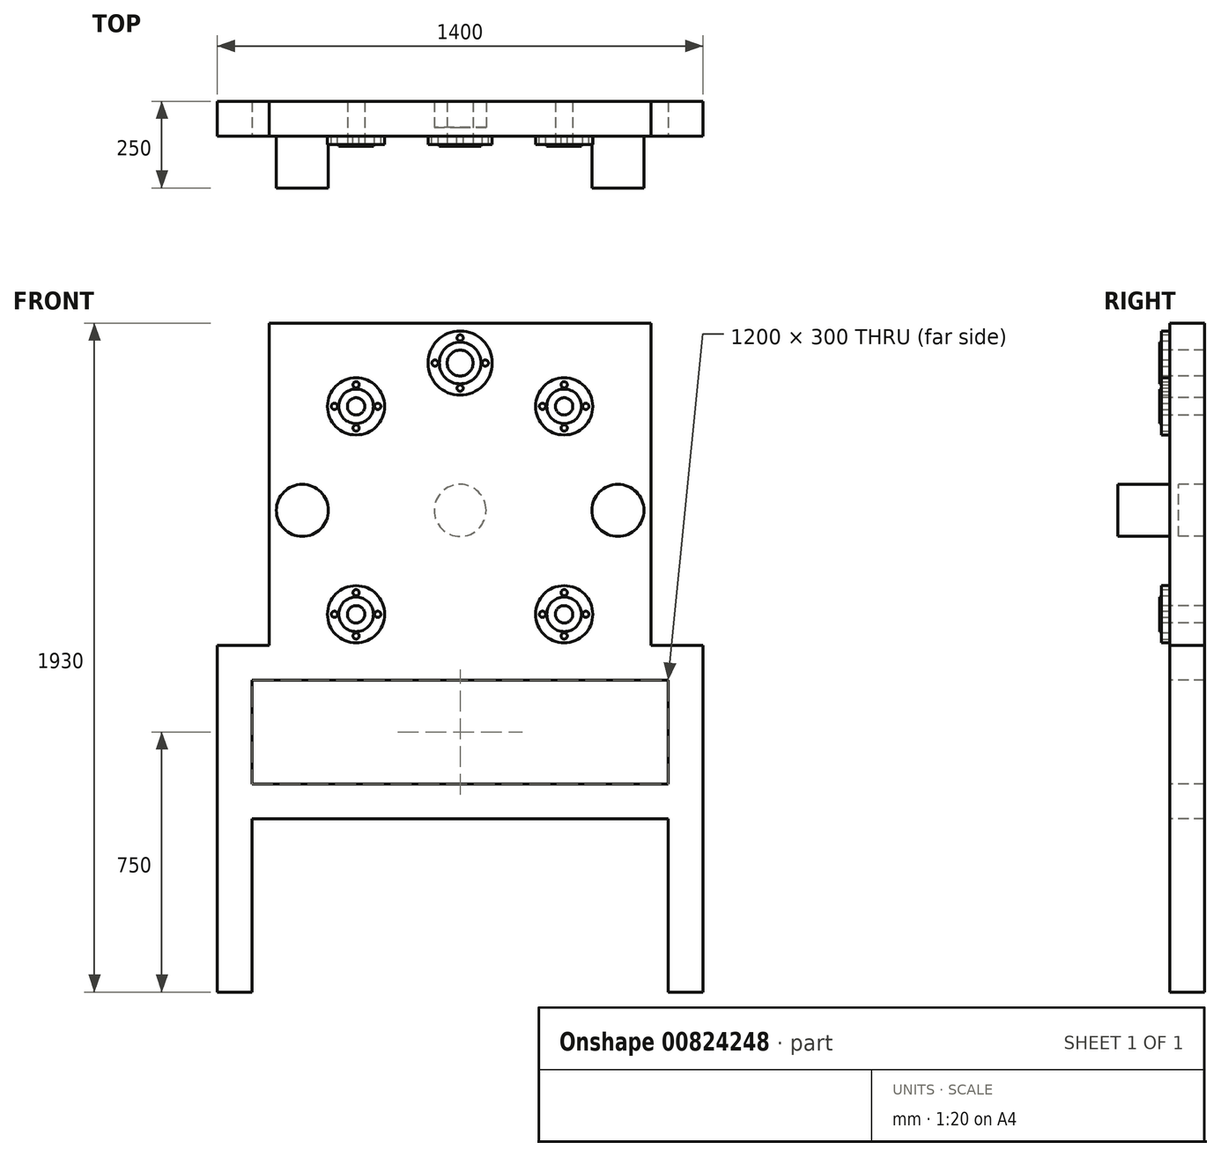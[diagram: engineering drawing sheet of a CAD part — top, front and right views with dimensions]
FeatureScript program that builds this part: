
annotation { "Feature Type Name" : "Feature", "Feature Type Description" : "" }
export const myFeature = defineFeature(function(context is Context, id is Id, definition is map)
    precondition{}
    {
        {
            var Q0;
            Q0=qCreatedBy(makeId("Front.planeOp"),FACE);
            var sketch = newSketch(context, id + "F0", { "sketchPlane" : qUnion([Q0])});
            skLineSegment(sketch, "E0.bottom", {"start": v(550, -965) * mm, "end": v(400, -965) * mm});
            skLineSegment(sketch, "E0.top", {"start": v(550, 965) * mm, "end": v(-550, 965) * mm});
            skLineSegment(sketch, "E0.left", {"start": v(550, -965) * mm, "end": v(550, 965) * mm});
            skLineSegment(sketch, "E0.right", {"start": v(-550, -965) * mm, "end": v(-550, 965) * mm});
            skPoint(sketch, "E0.middle", {"position": v(0, 0) * mm});
            skLineSegment(sketch, "E1.top", {"start": v(-400, -765) * mm, "end": v(400, -765) * mm});
            skLineSegment(sketch, "E1.left", {"start": v(-400, -965) * mm, "end": v(-400, -765) * mm});
            skLineSegment(sketch, "E1.right", {"start": v(400, -965) * mm, "end": v(400, -765) * mm});
            skLineSegment(sketch, "E2.bottom", {"start": v(-400, -615) * mm, "end": v(400, -615) * mm});
            skLineSegment(sketch, "E2.top", {"start": v(-400, -315) * mm, "end": v(400, -315) * mm});
            skLineSegment(sketch, "E2.left", {"start": v(-400, -615) * mm, "end": v(-400, -315) * mm});
            skLineSegment(sketch, "E2.right", {"start": v(400, -615) * mm, "end": v(400, -315) * mm});
            skLineSegment(sketch, "E3.trimOffspring", {"start": v(-400, -965) * mm, "end": v(-550, -965) * mm});
            skLineSegment(sketch, "E4.bottom", {"start": v(-400, -165) * mm, "end": v(400, -165) * mm});
            skLineSegment(sketch, "E4.top", {"start": v(-400, 35) * mm, "end": v(400, 35) * mm});
            skLineSegment(sketch, "E4.left", {"start": v(-400, -165) * mm, "end": v(-400, 35) * mm});
            skLineSegment(sketch, "E4.right", {"start": v(400, -165) * mm, "end": v(400, 35) * mm});
            skPoint(sketch, "E5.middle", {"position": v(0, 425) * mm});
            skSolve(sketch);
        }
        {
            var Q0;
            Q0=makeQuery(id+"F0.imprint","IMPRINT",FACE,{"disambiguationData":[TD([[makeQuery(id+"F0.imprint","IMPRINT",EDGE,{"derivedFrom":sQuery(id+"F0.wireOp",EDGE,"E0.bottom")}),-1.0]])]});
            extrude(context, id + "F1", {"entities" : qUnion([Q0]), "depth" : 100 * mm, "offsetDistance" : 25 * mm});
        }
        {
            var Q0;
            Q0=makeQuery(id+"F1.opExtrude","CAP_FACE",FACE,{"disambiguationData":[OSD([sQuery(id+"F0.wireOp",EDGE,"E0.bottom"),sQuery(id+"F0.wireOp",EDGE,"E0.top"),sQuery(id+"F0.wireOp",EDGE,"E0.left"),sQuery(id+"F0.wireOp",EDGE,"E0.right"),sQuery(id+"F0.wireOp",EDGE,"E1.top"),sQuery(id+"F0.wireOp",EDGE,"E1.left"),sQuery(id+"F0.wireOp",EDGE,"E1.right"),sQuery(id+"F0.wireOp",EDGE,"E2.bottom"),sQuery(id+"F0.wireOp",EDGE,"E2.top"),sQuery(id+"F0.wireOp",EDGE,"E2.left"),sQuery(id+"F0.wireOp",EDGE,"E2.right"),sQuery(id+"F0.wireOp",EDGE,"E3.trimOffspring"),sQuery(id+"F0.wireOp",EDGE,"nSGubIzk-R7de-6MO4-penA-cvBglKJnvsGC"),sQuery(id+"F0.wireOp",EDGE,"E4.bottom"),sQuery(id+"F0.wireOp",EDGE,"E4.top"),sQuery(id+"F0.wireOp",EDGE,"E4.left"),sQuery(id+"F0.wireOp",EDGE,"E4.right")])],"isStart":false});
            var sketch = newSketch(context, id + "F2", { "sketchPlane" : qUnion([Q0])});
            skCircle(sketch, "E6", {"center": v(-300, 125) * mm, "radius": 25 * mm});
            skCircle(sketch, "E7.0", {"center": v(0, 425) * mm, "radius": 75 * mm});
            skCircle(sketch, "E8.0.1.0", {"center": v(-300, 725) * mm, "radius": 25 * mm});
            skCircle(sketch, "E8.1.0.0", {"center": v(300, 125) * mm, "radius": 25 * mm});
            skCircle(sketch, "E8.1.1.0", {"center": v(300, 725) * mm, "radius": 25 * mm});
            skLineSegment(sketch, "E8.direction1", {"start": v(-300, 125) * mm, "end": v(300, 125) * mm, "construction": true});
            skLineSegment(sketch, "E8.direction2", {"start": v(-300, 125) * mm, "end": v(-300, 725) * mm, "construction": true});
            skSolve(sketch);
        }
        {
            var Q0;
            Q0=qSketchRegion(id+"F2",true);
            extrude(context, id + "F3", {"entities" : qUnion([Q0]), "operationType" : NewBodyOperationType.REMOVE, "oppositeDirection" : true, "depth" : 100 * mm, "offsetDistance" : 25 * mm});
        }
        {
            var Q0;
            Q0=makeQuery(id+"F1.opExtrude","CAP_FACE",FACE,{"disambiguationData":[OSD([sQuery(id+"F0.wireOp",EDGE,"E0.bottom"),sQuery(id+"F0.wireOp",EDGE,"E0.top"),sQuery(id+"F0.wireOp",EDGE,"E0.left"),sQuery(id+"F0.wireOp",EDGE,"E0.right"),sQuery(id+"F0.wireOp",EDGE,"E1.top"),sQuery(id+"F0.wireOp",EDGE,"E1.left"),sQuery(id+"F0.wireOp",EDGE,"E1.right"),sQuery(id+"F0.wireOp",EDGE,"E2.bottom"),sQuery(id+"F0.wireOp",EDGE,"E2.top"),sQuery(id+"F0.wireOp",EDGE,"E2.left"),sQuery(id+"F0.wireOp",EDGE,"E2.right"),sQuery(id+"F0.wireOp",EDGE,"E3.trimOffspring"),sQuery(id+"F0.wireOp",EDGE,"nSGubIzk-R7de-6MO4-penA-cvBglKJnvsGC"),sQuery(id+"F0.wireOp",EDGE,"E4.bottom"),sQuery(id+"F0.wireOp",EDGE,"E4.top"),sQuery(id+"F0.wireOp",EDGE,"E4.left"),sQuery(id+"F0.wireOp",EDGE,"E4.right")])],"isStart":false});
            var sketch = newSketch(context, id + "F4", { "sketchPlane" : qUnion([Q0])});
            skCircle(sketch, "E9", {"center": v(-455, 425) * mm, "radius": 75 * mm});
            skCircle(sketch, "E10.MirrorC", {"center": v(455, 425) * mm, "radius": 75 * mm});
            skSolve(sketch);
        }
        {
            var Q0;
            Q0=qSketchRegion(id+"F4",true);
            extrude(context, id + "F5", {"entities" : qUnion([Q0]), "operationType" : NewBodyOperationType.ADD, "depth" : 150 * mm, "offsetDistance" : 25 * mm});
        }
        {
            var Q0;
            Q0=makeQuery(id+"F1.opExtrude","CAP_FACE",FACE,{"disambiguationData":[OSD([sQuery(id+"F0.wireOp",EDGE,"E0.bottom"),sQuery(id+"F0.wireOp",EDGE,"E0.top"),sQuery(id+"F0.wireOp",EDGE,"E0.left"),sQuery(id+"F0.wireOp",EDGE,"E0.right"),sQuery(id+"F0.wireOp",EDGE,"E1.top"),sQuery(id+"F0.wireOp",EDGE,"E1.left"),sQuery(id+"F0.wireOp",EDGE,"E1.right"),sQuery(id+"F0.wireOp",EDGE,"E2.bottom"),sQuery(id+"F0.wireOp",EDGE,"E2.top"),sQuery(id+"F0.wireOp",EDGE,"E2.left"),sQuery(id+"F0.wireOp",EDGE,"E2.right"),sQuery(id+"F0.wireOp",EDGE,"E3.trimOffspring"),sQuery(id+"F0.wireOp",EDGE,"nSGubIzk-R7de-6MO4-penA-cvBglKJnvsGC"),sQuery(id+"F0.wireOp",EDGE,"E4.bottom"),sQuery(id+"F0.wireOp",EDGE,"E4.top"),sQuery(id+"F0.wireOp",EDGE,"E4.left"),sQuery(id+"F0.wireOp",EDGE,"E4.right")])],"isStart":false});
            var sketch = newSketch(context, id + "F6", { "sketchPlane" : qUnion([Q0])});
            skCircle(sketch, "E11", {"center": v(-300, 725) * mm, "radius": 82.5 * mm});
            skCircle(sketch, "E12", {"center": v(-300, 787.5) * mm, "radius": 9 * mm});
            skCircle(sketch, "E13.0", {"center": v(-300, 725) * mm, "radius": 25 * mm});
            skCircle(sketch, "E14.1.0", {"center": v(-362.5, 725) * mm, "radius": 9 * mm});
            skCircle(sketch, "E14.2.0", {"center": v(-300, 662.5) * mm, "radius": 9 * mm});
            skCircle(sketch, "E14.3.0", {"center": v(-237.5, 725) * mm, "radius": 9 * mm});
            skPoint(sketch, "E15.0.1.0", {"position": v(-300, 125) * mm});
            skCircle(sketch, "E15.0.1.1", {"center": v(-300, 125) * mm, "radius": 82.5 * mm});
            skCircle(sketch, "E15.0.1.2", {"center": v(-300, 125) * mm, "radius": 25 * mm});
            skCircle(sketch, "E15.0.1.3", {"center": v(-237.5, 125) * mm, "radius": 9 * mm});
            skCircle(sketch, "E15.0.1.4", {"center": v(-362.5, 125) * mm, "radius": 9 * mm});
            skCircle(sketch, "E15.0.1.5", {"center": v(-300, 187.5) * mm, "radius": 9 * mm});
            skCircle(sketch, "E15.0.1.6", {"center": v(-300, 62.5) * mm, "radius": 9 * mm});
            skPoint(sketch, "E15.1.0.0", {"position": v(300, 725) * mm});
            skCircle(sketch, "E15.1.0.1", {"center": v(300, 725) * mm, "radius": 82.5 * mm});
            skCircle(sketch, "E15.1.0.2", {"center": v(300, 725) * mm, "radius": 25 * mm});
            skCircle(sketch, "E15.1.0.3", {"center": v(362.5, 725) * mm, "radius": 9 * mm});
            skCircle(sketch, "E15.1.0.4", {"center": v(237.5, 725) * mm, "radius": 9 * mm});
            skCircle(sketch, "E15.1.0.5", {"center": v(300, 787.5) * mm, "radius": 9 * mm});
            skCircle(sketch, "E15.1.0.6", {"center": v(300, 662.5) * mm, "radius": 9 * mm});
            skPoint(sketch, "E15.1.1.0", {"position": v(300, 125) * mm});
            skCircle(sketch, "E15.1.1.1", {"center": v(300, 125) * mm, "radius": 82.5 * mm});
            skCircle(sketch, "E15.1.1.2", {"center": v(300, 125) * mm, "radius": 25 * mm});
            skCircle(sketch, "E15.1.1.3", {"center": v(362.5, 125) * mm, "radius": 9 * mm});
            skCircle(sketch, "E15.1.1.4", {"center": v(237.5, 125) * mm, "radius": 9 * mm});
            skCircle(sketch, "E15.1.1.5", {"center": v(300, 187.5) * mm, "radius": 9 * mm});
            skCircle(sketch, "E15.1.1.6", {"center": v(300, 62.5) * mm, "radius": 9 * mm});
            skLineSegment(sketch, "E15.direction1", {"start": v(-300, 662.5) * mm, "end": v(300, 662.5) * mm, "construction": true});
            skLineSegment(sketch, "E15.direction2", {"start": v(-300, 662.5) * mm, "end": v(-300, 62.5) * mm, "construction": true});
            skSolve(sketch);
        }
        {
            var Q0;
            Q0=qSketchRegion(id+"F6",true);
            extrude(context, id + "F7", {"entities" : qUnion([Q0]), "operationType" : NewBodyOperationType.ADD, "depth" : 25 * mm, "offsetDistance" : 25 * mm});
        }
        {
            var Q0;
            Q0=makeQuery(id+"F7.opExtrude","CAP_FACE",FACE,{"disambiguationData":[OSD([sQuery(id+"F6.wireOp",EDGE,"E11"),sQuery(id+"F6.wireOp",EDGE,"E12"),sQuery(id+"F6.wireOp",EDGE,"E13.0"),sQuery(id+"F6.wireOp",EDGE,"E14.1.0"),sQuery(id+"F6.wireOp",EDGE,"E14.2.0"),sQuery(id+"F6.wireOp",EDGE,"E14.3.0")])],"isStart":false});
            var sketch = newSketch(context, id + "F8", { "sketchPlane" : qUnion([Q0])});
            skCircle(sketch, "E16", {"center": v(-300, 725) * mm, "radius": 50 * mm});
            skCircle(sketch, "E17.0.1.0", {"center": v(-300, 125) * mm, "radius": 50 * mm});
            skCircle(sketch, "E17.1.0.0", {"center": v(300, 725) * mm, "radius": 50 * mm});
            skCircle(sketch, "E17.1.1.0", {"center": v(300, 125) * mm, "radius": 50 * mm});
            skLineSegment(sketch, "E17.direction1", {"start": v(-300, 725) * mm, "end": v(300, 725) * mm, "construction": true});
            skLineSegment(sketch, "E17.direction2", {"start": v(-300, 725) * mm, "end": v(-300, 125) * mm, "construction": true});
            skCircle(sketch, "E18", {"center": v(300, 725) * mm, "radius": 25 * mm});
            skCircle(sketch, "E19", {"center": v(300, 125) * mm, "radius": 25 * mm});
            skCircle(sketch, "E20", {"center": v(-300, 125) * mm, "radius": 25 * mm});
            skCircle(sketch, "E21", {"center": v(-300, 725) * mm, "radius": 25 * mm});
            skSolve(sketch);
        }
        {
            var Q0;
            Q0=qSketchRegion(id+"F8",true);
            extrude(context, id + "F9", {"entities" : qUnion([Q0]), "operationType" : NewBodyOperationType.ADD, "depth" : 5 * mm, "offsetDistance" : 25 * mm});
        }
        {
            var Q0;
            {var subQ0=sQuery(id+"F0.wireOp",EDGE,"E4.right");var subQ1=sQuery(id+"F0.wireOp",EDGE,"E4.left");var subQ2=sQuery(id+"F0.wireOp",EDGE,"E4.top");var subQ3=sQuery(id+"F0.wireOp",EDGE,"E1.left");var subQ4=sQuery(id+"F0.wireOp",EDGE,"E4.bottom");var subQ5=sQuery(id+"F0.wireOp",EDGE,"E3.trimOffspring");var subQ6=sQuery(id+"F0.wireOp",EDGE,"E2.right");var subQ7=sQuery(id+"F0.wireOp",EDGE,"E0.left");var subQ8=sQuery(id+"F0.wireOp",EDGE,"E0.top");var subQ9=sQuery(id+"F0.wireOp",EDGE,"E0.right");var subQ10=sQuery(id+"F0.wireOp",EDGE,"E2.bottom");var subQ11=sQuery(id+"F0.wireOp",EDGE,"E0.bottom");var subQ12=sQuery(id+"F0.wireOp",EDGE,"E2.left");var subQ13=sQuery(id+"F0.wireOp",EDGE,"E1.top");var subQ14=sQuery(id+"F0.wireOp",EDGE,"E1.right");var subQ15=sQuery(id+"F0.wireOp",EDGE,"E2.top");Q0=makeQuery(id+"F7.boolean.opBoolean","SPLIT",FACE,{"disambiguationData":[TD([makeQuery(id+"F1.opExtrude","SWEPT_FACE",FACE,{"disambiguationData":[OSD([subQ11])]})])],"derivedFrom":makeQuery(id+"F1.opExtrude","CAP_FACE",FACE,{"disambiguationData":[OSD([subQ11,subQ8,subQ7,subQ9,subQ13,subQ3,subQ14,subQ10,subQ15,subQ12,subQ6,subQ5,subQ4,subQ2,subQ1,subQ0])],"isStart":false})});}
            var sketch = newSketch(context, id + "F10", { "sketchPlane" : qUnion([Q0])});
            skCircle(sketch, "E22.0", {"center": v(0, 425) * mm, "radius": 75 * mm});
            skSolve(sketch);
        }
        {
            var Q0;
            Q0=qSketchRegion(id+"F10",true);
            extrude(context, id + "F11", {"entities" : qUnion([Q0]), "operationType" : NewBodyOperationType.ADD, "oppositeDirection" : true, "depth" : 25 * mm, "offsetDistance" : 25 * mm});
        }
        {
            var Q0;
            {var subQ0=sQuery(id+"F0.wireOp",EDGE,"E4.right");var subQ1=sQuery(id+"F0.wireOp",EDGE,"E4.left");var subQ2=sQuery(id+"F0.wireOp",EDGE,"E4.top");var subQ3=sQuery(id+"F0.wireOp",EDGE,"E1.left");var subQ4=sQuery(id+"F0.wireOp",EDGE,"E4.bottom");var subQ5=sQuery(id+"F0.wireOp",EDGE,"E3.trimOffspring");var subQ6=sQuery(id+"F0.wireOp",EDGE,"E2.right");var subQ7=sQuery(id+"F0.wireOp",EDGE,"E0.left");var subQ8=sQuery(id+"F0.wireOp",EDGE,"E0.top");var subQ9=sQuery(id+"F0.wireOp",EDGE,"E0.right");var subQ10=sQuery(id+"F0.wireOp",EDGE,"E2.bottom");var subQ11=sQuery(id+"F0.wireOp",EDGE,"E0.bottom");var subQ12=sQuery(id+"F0.wireOp",EDGE,"E2.left");var subQ13=sQuery(id+"F0.wireOp",EDGE,"E1.top");var subQ14=sQuery(id+"F0.wireOp",EDGE,"E1.right");var subQ15=sQuery(id+"F0.wireOp",EDGE,"E2.top");Q0=makeQuery(id+"F11.boolean.opBoolean","MERGE",FACE,{"derivedFrom":[makeQuery(id+"F7.boolean.opBoolean","SPLIT",FACE,{"disambiguationData":[TD([makeQuery(id+"F1.opExtrude","SWEPT_FACE",FACE,{"disambiguationData":[OSD([subQ11])]})])],"derivedFrom":makeQuery(id+"F1.opExtrude","CAP_FACE",FACE,{"disambiguationData":[OSD([subQ11,subQ8,subQ7,subQ9,subQ13,subQ3,subQ14,subQ10,subQ15,subQ12,subQ6,subQ5,subQ4,subQ2,subQ1,subQ0])],"isStart":false})}),makeQuery(id+"F11.opExtrude","CAP_FACE",FACE,{"disambiguationData":[OSD([sQuery(id+"F10.wireOp",EDGE,"E22.0")])],"isStart":true})]});}
            var sketch = newSketch(context, id + "F12", { "sketchPlane" : qUnion([Q0])});
            skCircle(sketch, "E23", {"center": v(0, 850) * mm, "radius": 37.5 * mm});
            skPoint(sketch, "E23.centerSnap0", {"position": v(0, 965) * mm});
            skCircle(sketch, "E24.0", {"center": v(300, 725) * mm, "radius": 25 * mm});
            skSolve(sketch);
        }
        {
            var Q0;
            Q0=makeQuery(id+"F12.imprint","IMPRINT",FACE,{"disambiguationData":[TD([[makeQuery(id+"F12.imprint","IMPRINT",EDGE,{"derivedFrom":sQuery(id+"F12.wireOp",EDGE,"E23")}),1.0]])]});
            extrude(context, id + "F13", {"entities" : qUnion([Q0]), "operationType" : NewBodyOperationType.REMOVE, "oppositeDirection" : true, "depth" : 100 * mm, "offsetDistance" : 25 * mm});
        }
        {
            var Q0;
            {var subQ0=sQuery(id+"F0.wireOp",EDGE,"E4.right");var subQ1=sQuery(id+"F0.wireOp",EDGE,"E4.left");var subQ2=sQuery(id+"F0.wireOp",EDGE,"E4.top");var subQ3=sQuery(id+"F0.wireOp",EDGE,"E1.left");var subQ4=sQuery(id+"F0.wireOp",EDGE,"E4.bottom");var subQ5=sQuery(id+"F0.wireOp",EDGE,"E3.trimOffspring");var subQ6=sQuery(id+"F0.wireOp",EDGE,"E2.right");var subQ7=sQuery(id+"F0.wireOp",EDGE,"E0.left");var subQ8=sQuery(id+"F0.wireOp",EDGE,"E0.top");var subQ9=sQuery(id+"F0.wireOp",EDGE,"E0.right");var subQ10=sQuery(id+"F0.wireOp",EDGE,"E2.bottom");var subQ11=sQuery(id+"F0.wireOp",EDGE,"E0.bottom");var subQ12=sQuery(id+"F0.wireOp",EDGE,"E2.left");var subQ13=sQuery(id+"F0.wireOp",EDGE,"E1.top");var subQ14=sQuery(id+"F0.wireOp",EDGE,"E1.right");var subQ15=sQuery(id+"F0.wireOp",EDGE,"E2.top");Q0=makeQuery(id+"F11.boolean.opBoolean","MERGE",FACE,{"derivedFrom":[makeQuery(id+"F7.boolean.opBoolean","SPLIT",FACE,{"disambiguationData":[TD([makeQuery(id+"F1.opExtrude","SWEPT_FACE",FACE,{"disambiguationData":[OSD([subQ11])]})])],"derivedFrom":makeQuery(id+"F1.opExtrude","CAP_FACE",FACE,{"disambiguationData":[OSD([subQ11,subQ8,subQ7,subQ9,subQ13,subQ3,subQ14,subQ10,subQ15,subQ12,subQ6,subQ5,subQ4,subQ2,subQ1,subQ0])],"isStart":false})}),makeQuery(id+"F11.opExtrude","CAP_FACE",FACE,{"disambiguationData":[OSD([sQuery(id+"F10.wireOp",EDGE,"E22.0")])],"isStart":true})]});}
            var sketch = newSketch(context, id + "F14", { "sketchPlane" : qUnion([Q0])});
            skCircle(sketch, "E25", {"center": v(0, 850) * mm, "radius": 92.5 * mm});
            skCircle(sketch, "E26", {"center": v(0, 922.5) * mm, "radius": 9 * mm});
            skCircle(sketch, "E27.1.0", {"center": v(-72.5, 850) * mm, "radius": 9 * mm});
            skCircle(sketch, "E27.2.0", {"center": v(0, 777.5) * mm, "radius": 9 * mm});
            skCircle(sketch, "E27.3.0", {"center": v(72.5, 850) * mm, "radius": 9 * mm});
            skSolve(sketch);
        }
        {
            var Q0;
            Q0=makeQuery(id+"F14.imprint","IMPRINT",FACE,{"disambiguationData":[TD([[makeQuery(id+"F14.imprint","IMPRINT",EDGE,{"derivedFrom":sQuery(id+"F14.wireOp",EDGE,"E25")}),1.0]])]});
            extrude(context, id + "F15", {"entities" : qUnion([Q0]), "operationType" : NewBodyOperationType.ADD, "depth" : 25 * mm, "offsetDistance" : 25 * mm});
        }
        {
            var Q0;
            Q0=makeQuery(id+"F15.opExtrude","CAP_FACE",FACE,{"disambiguationData":[OSD([sQuery(id+"F12.wireOp",EDGE,"E23"),sQuery(id+"F14.wireOp",EDGE,"E25"),sQuery(id+"F14.wireOp",EDGE,"E26"),sQuery(id+"F14.wireOp",EDGE,"E27.1.0"),sQuery(id+"F14.wireOp",EDGE,"E27.2.0"),sQuery(id+"F14.wireOp",EDGE,"E27.3.0")])],"isStart":false});
            var sketch = newSketch(context, id + "F16", { "sketchPlane" : qUnion([Q0])});
            skCircle(sketch, "E28", {"center": v(0, 850) * mm, "radius": 60 * mm});
            skSolve(sketch);
        }
        {
            var Q0;
            Q0=makeQuery(id+"F16.imprint","IMPRINT",FACE,{"disambiguationData":[TD([[makeQuery(id+"F16.imprint","IMPRINT",EDGE,{"derivedFrom":sQuery(id+"F16.wireOp",EDGE,"E28")}),1.0]])]});
            extrude(context, id + "F17", {"entities" : qUnion([Q0]), "operationType" : NewBodyOperationType.ADD, "depth" : 5 * mm, "offsetDistance" : 25 * mm});
        }
        {
            var Q0;
            {var subQ2=sQuery(id+"F0.wireOp",EDGE,"E4.right");var subQ5=sQuery(id+"F0.wireOp",EDGE,"E4.left");var subQ8=sQuery(id+"F0.wireOp",EDGE,"E4.top");var subQ10=sQuery(id+"F0.wireOp",EDGE,"E4.bottom");var subQ12=sQuery(id+"F0.wireOp",EDGE,"E3.trimOffspring");var subQ14=sQuery(id+"F0.wireOp",EDGE,"E2.right");var subQ16=sQuery(id+"F0.wireOp",EDGE,"E0.left");var subQ18=sQuery(id+"F0.wireOp",EDGE,"E0.top");var subQ20=sQuery(id+"F0.wireOp",EDGE,"E0.right");var subQ23=sQuery(id+"F0.wireOp",EDGE,"E2.bottom");var subQ25=sQuery(id+"F0.wireOp",EDGE,"E0.bottom");var subQ26=makeQuery(id+"F1.opExtrude","SWEPT_FACE",FACE,{"disambiguationData":[OSD([subQ25])]});var subQ27=sQuery(id+"F0.wireOp",EDGE,"E2.left");var subQ29=sQuery(id+"F0.wireOp",EDGE,"E1.top");var subQ32=sQuery(id+"F0.wireOp",EDGE,"E1.left");var subQ34=sQuery(id+"F0.wireOp",EDGE,"E1.right");var subQ36=sQuery(id+"F0.wireOp",EDGE,"E2.top");Q0=makeQuery(id+"F15.boolean.opBoolean","SPLIT",FACE,{"disambiguationData":[TD([subQ26])],"derivedFrom":makeQuery(id+"F11.boolean.opBoolean","MERGE",FACE,{"derivedFrom":[makeQuery(id+"F7.boolean.opBoolean","SPLIT",FACE,{"disambiguationData":[TD([subQ26])],"derivedFrom":makeQuery(id+"F1.opExtrude","CAP_FACE",FACE,{"disambiguationData":[OSD([subQ25,subQ18,subQ16,subQ20,subQ29,subQ32,subQ34,subQ23,subQ36,subQ27,subQ14,subQ12,subQ10,subQ8,subQ5,subQ2])],"isStart":false})}),makeQuery(id+"F11.opExtrude","CAP_FACE",FACE,{"disambiguationData":[OSD([sQuery(id+"F10.wireOp",EDGE,"E22.0")])],"isStart":true})]})});}
            var sketch = newSketch(context, id + "F18", { "sketchPlane" : qUnion([Q0])});
            skLineSegment(sketch, "E29.bottom", {"start": v(-568.84, 35) * mm, "end": v(631.16, 35) * mm});
            skLineSegment(sketch, "E29.top", {"start": v(-568.84, -965) * mm, "end": v(631.16, -965) * mm});
            skLineSegment(sketch, "E29.left", {"start": v(-568.84, 35) * mm, "end": v(-568.84, -965) * mm});
            skLineSegment(sketch, "E29.right", {"start": v(631.16, 35) * mm, "end": v(631.16, -965) * mm});
            skSolve(sketch);
        }
        {
            var Q0;
            Q0 = qSketchRegion(id + "F18", true);
            extrude(context, id + "F19", {"entities" : qUnion([Q0]), "operationType" : NewBodyOperationType.REMOVE, "oppositeDirection" : true, "depth" : 100 * mm, "offsetDistance" : 25 * mm});
        }
        {
            var Q0;
            Q0=makeQuery(id+"F19.boolean.opBoolean","MERGE",FACE,{"derivedFrom":[makeQuery(id+"F1.opExtrude","SWEPT_FACE",FACE,{"disambiguationData":[OSD([sQuery(id+"F0.wireOp",EDGE,"E4.top")])]}),makeQuery(id+"F19.opExtrude","SWEPT_FACE",FACE,{"disambiguationData":[OSD([sQuery(id+"F18.wireOp",EDGE,"E29.bottom")])]})]});
            var sketch = newSketch(context, id + "F20", { "sketchPlane" : qUnion([Q0])});
            skLineSegment(sketch, "E30.bottom", {"start": v(-700, 0) * mm, "end": v(700, 0) * mm});
            skLineSegment(sketch, "E30.top", {"start": v(-700, 100) * mm, "end": v(700, 100) * mm});
            skLineSegment(sketch, "E30.left", {"start": v(-700, 0) * mm, "end": v(-700, 100) * mm});
            skLineSegment(sketch, "E30.right", {"start": v(700, 0) * mm, "end": v(700, 100) * mm});
            skSolve(sketch);
        }
        {
            var Q0;
            Q0 = qSketchRegion(id + "F20", true);
            extrude(context, id + "F21", {"entities" : qUnion([Q0]), "operationType" : NewBodyOperationType.ADD, "depth" : 100 * mm, "offsetDistance" : 25 * mm});
        }
        {
            var Q0;
            {var subQ2=sQuery(id+"F0.wireOp",EDGE,"E4.right");var subQ5=sQuery(id+"F0.wireOp",EDGE,"E4.left");var subQ8=sQuery(id+"F0.wireOp",EDGE,"E4.top");var subQ10=sQuery(id+"F0.wireOp",EDGE,"E4.bottom");var subQ12=sQuery(id+"F0.wireOp",EDGE,"E3.trimOffspring");var subQ14=sQuery(id+"F0.wireOp",EDGE,"E2.right");var subQ16=sQuery(id+"F0.wireOp",EDGE,"E0.left");var subQ18=sQuery(id+"F0.wireOp",EDGE,"E0.top");var subQ20=sQuery(id+"F0.wireOp",EDGE,"E0.right");var subQ23=sQuery(id+"F0.wireOp",EDGE,"E2.bottom");var subQ25=sQuery(id+"F0.wireOp",EDGE,"E0.bottom");var subQ26=makeQuery(id+"F1.opExtrude","SWEPT_FACE",FACE,{"disambiguationData":[OSD([subQ25])]});var subQ27=sQuery(id+"F0.wireOp",EDGE,"E2.left");var subQ29=sQuery(id+"F0.wireOp",EDGE,"E1.top");var subQ32=sQuery(id+"F0.wireOp",EDGE,"E1.left");var subQ34=sQuery(id+"F0.wireOp",EDGE,"E1.right");var subQ36=sQuery(id+"F0.wireOp",EDGE,"E2.top");Q0=makeQuery(id+"F21.boolean.opBoolean","MERGE",FACE,{"derivedFrom":[makeQuery(id+"F15.boolean.opBoolean","SPLIT",FACE,{"disambiguationData":[TD([subQ26])],"derivedFrom":makeQuery(id+"F11.boolean.opBoolean","MERGE",FACE,{"derivedFrom":[makeQuery(id+"F7.boolean.opBoolean","SPLIT",FACE,{"disambiguationData":[TD([subQ26])],"derivedFrom":makeQuery(id+"F1.opExtrude","CAP_FACE",FACE,{"disambiguationData":[OSD([subQ25,subQ18,subQ16,subQ20,subQ29,subQ32,subQ34,subQ23,subQ36,subQ27,subQ14,subQ12,subQ10,subQ8,subQ5,subQ2])],"isStart":false})}),makeQuery(id+"F11.opExtrude","CAP_FACE",FACE,{"disambiguationData":[OSD([sQuery(id+"F10.wireOp",EDGE,"E22.0")])],"isStart":true})]})}),makeQuery(id+"F21.opExtrude","SWEPT_FACE",FACE,{"disambiguationData":[OSD([sQuery(id+"F20.wireOp",EDGE,"E30.top")])]})]});}
            var sketch = newSketch(context, id + "F22", { "sketchPlane" : qUnion([Q0])});
            skLineSegment(sketch, "E31.bottom", {"start": v(-700, -65) * mm, "end": v(-600, -65) * mm});
            skLineSegment(sketch, "E31.top", {"start": v(-700, -965) * mm, "end": v(-600, -965) * mm});
            skLineSegment(sketch, "E31.left", {"start": v(-700, -65) * mm, "end": v(-700, -965) * mm});
            skLineSegment(sketch, "E31.right", {"start": v(700, -65) * mm, "end": v(700, -965) * mm});
            skLineSegment(sketch, "E32.top", {"start": v(-600, -465) * mm, "end": v(600, -465) * mm});
            skLineSegment(sketch, "E32.left", {"start": v(-600, -965) * mm, "end": v(-600, -465) * mm});
            skLineSegment(sketch, "E32.right", {"start": v(600, -965) * mm, "end": v(600, -465) * mm});
            skLineSegment(sketch, "E33.bottom", {"start": v(-600, -365) * mm, "end": v(600, -365) * mm});
            skLineSegment(sketch, "E33.left", {"start": v(-600, -365) * mm, "end": v(-600, -65) * mm});
            skLineSegment(sketch, "E33.right", {"start": v(600, -365) * mm, "end": v(600, -65) * mm});
            skLineSegment(sketch, "E34.trimOffspring", {"start": v(600, -965) * mm, "end": v(700, -965) * mm});
            skLineSegment(sketch, "E35.trimOffspring", {"start": v(600, -65) * mm, "end": v(700, -65) * mm});
            skSolve(sketch);
        }
        {
            var Q0;
            Q0=makeQuery(id+"F22.imprint","IMPRINT",FACE,{"disambiguationData":[TD([[makeQuery(id+"F22.imprint","IMPRINT",EDGE,{"derivedFrom":sQuery(id+"F22.wireOp",EDGE,"E31.bottom")}),-1.0]])]});
            extrude(context, id + "F23", {"entities" : qUnion([Q0]), "operationType" : NewBodyOperationType.ADD, "oppositeDirection" : true, "depth" : 100 * mm, "offsetDistance" : 25 * mm});
        }
    });
